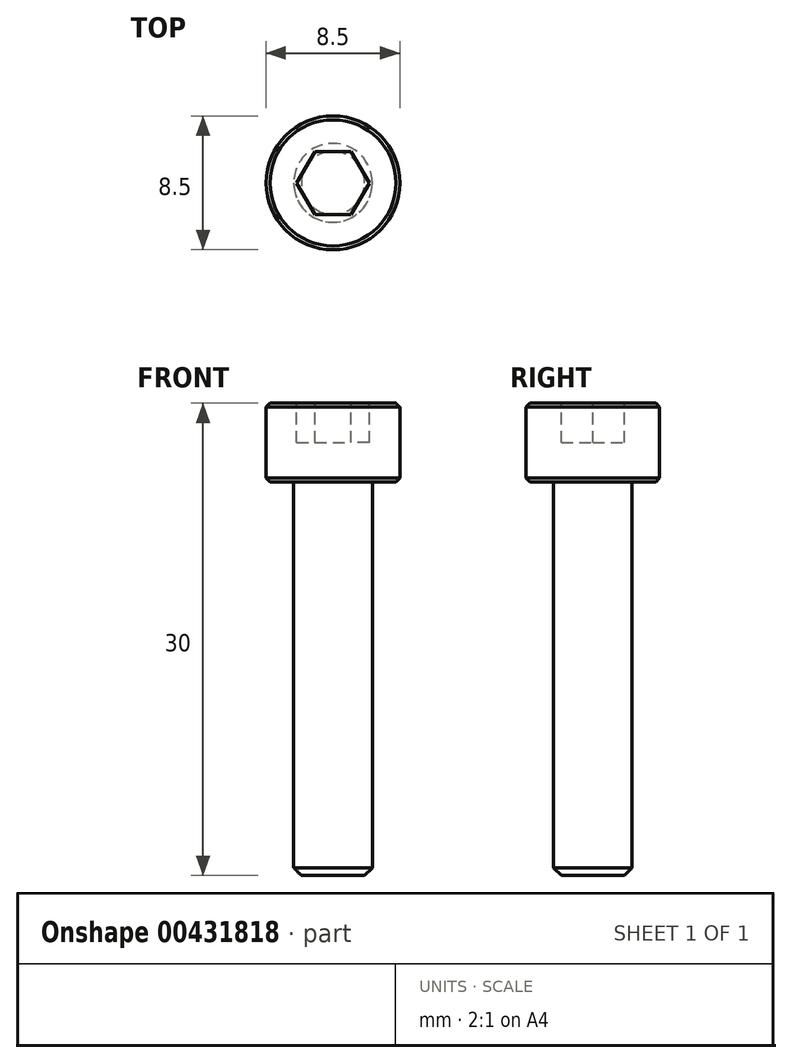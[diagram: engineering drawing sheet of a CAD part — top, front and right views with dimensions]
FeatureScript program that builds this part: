
annotation { "Feature Type Name" : "Feature", "Feature Type Description" : "" }
export const myFeature = defineFeature(function(context is Context, id is Id, definition is map)
    precondition{}
    {
        {
            var Q0;
            Q0=qCreatedBy(makeId("Front.planeOp"),FACE);
            var sketch = newSketch(context, id + "F0", { "sketchPlane" : qUnion([Q0])});
            skLineSegment(sketch, "E0", {"start": v(0, 0) * mm, "end": v(4.25, 0) * mm});
            skLineSegment(sketch, "E1", {"start": v(4.25, 0) * mm, "end": v(4.25, -5) * mm});
            skLineSegment(sketch, "E2", {"start": v(4.25, -5) * mm, "end": v(2.5, -5) * mm});
            skLineSegment(sketch, "E3", {"start": v(2.5, -5) * mm, "end": v(2.5, -30) * mm});
            skLineSegment(sketch, "E4", {"start": v(2.5, -30) * mm, "end": v(0, -30) * mm});
            skLineSegment(sketch, "E5", {"start": v(0, 0) * mm, "end": v(0, -30) * mm});
            skLineSegment(sketch, "E6", {"start": v(0, 0) * mm, "end": v(0, 2.24) * mm, "construction": true});
            skSolve(sketch);
        }
        {
            var Q0;
            Q0=qSketchRegion(id+"F0",true);
            var Q1;
            Q1=sQuery(id+"F0.wireOp",EDGE,"E5");
            revolve(context, id + "F1", {"entities" : qUnion([Q0]), "axis" : qUnion([Q1]), "revolveType" : RevolveType.FULL});
        }
        {
            var Q0;
            Q0=makeQuery(id+"F1.opRevolve","SWEPT_FACE",FACE,{"disambiguationData":[OSD([sQuery(id+"F0.wireOp",EDGE,"E0")])]});
            var sketch = newSketch(context, id + "F2", { "sketchPlane" : qUnion([Q0])});
            skCircle(sketch, "E7.cCircle", {"center": v(0, 0) * mm, "radius": 2 * mm, "construction": true});
            skLineSegment(sketch, "E7.0", {"start": v(-1.15, 2) * mm, "end": v(1.15, 2) * mm});
            skLineSegment(sketch, "E7.1", {"start": v(1.15, 2) * mm, "end": v(2.3, 0) * mm});
            skLineSegment(sketch, "E7.2", {"start": v(2.3, 0) * mm, "end": v(1.15, -2) * mm});
            skLineSegment(sketch, "E7.3", {"start": v(1.15, -2) * mm, "end": v(-1.15, -2) * mm});
            skLineSegment(sketch, "E7.4", {"start": v(-1.15, -2) * mm, "end": v(-2.3, 0) * mm});
            skLineSegment(sketch, "E7.5", {"start": v(-2.3, 0) * mm, "end": v(-1.15, 2) * mm});
            skPoint(sketch, "E7.0.midPoint", {"position": v(0, 2) * mm});
            skSolve(sketch);
        }
        {
            var Q0;
            Q0=qSketchRegion(id+"F2",true);
            extrude(context, id + "F3", {"entities" : qUnion([Q0]), "operationType" : NewBodyOperationType.REMOVE, "oppositeDirection" : true, "depth" : 2.5 * mm});
        }
        {
            var Q0;
            Q0=makeQuery(id+"F1.opRevolve","SWEPT_EDGE",EDGE,{"disambiguationData":[OSD([sQuery(id+"F0.wireOp",EDGE,"E3"),sQuery(id+"F0.wireOp",EDGE,"E4")])]});
            chamfer(context, id + "F4", {"entities" : qUnion([Q0]), "width" : 0.5 * mm, "tangentPropagation" : true});
        }
        {
            var Q0;
            Q0=makeQuery(id+"F1.opRevolve","SWEPT_EDGE",EDGE,{"disambiguationData":[OSD([sQuery(id+"F0.wireOp",EDGE,"E0"),sQuery(id+"F0.wireOp",EDGE,"E1")])]});
            var Q1;
            Q1=makeQuery(id+"F1.opRevolve","SWEPT_EDGE",EDGE,{"disambiguationData":[OSD([sQuery(id+"F0.wireOp",EDGE,"E1"),sQuery(id+"F0.wireOp",EDGE,"E2")])]});
            chamfer(context, id + "F5", {"entities" : qUnion([Q0, Q1]), "width" : 0.25 * mm, "tangentPropagation" : true});
        }
    });
